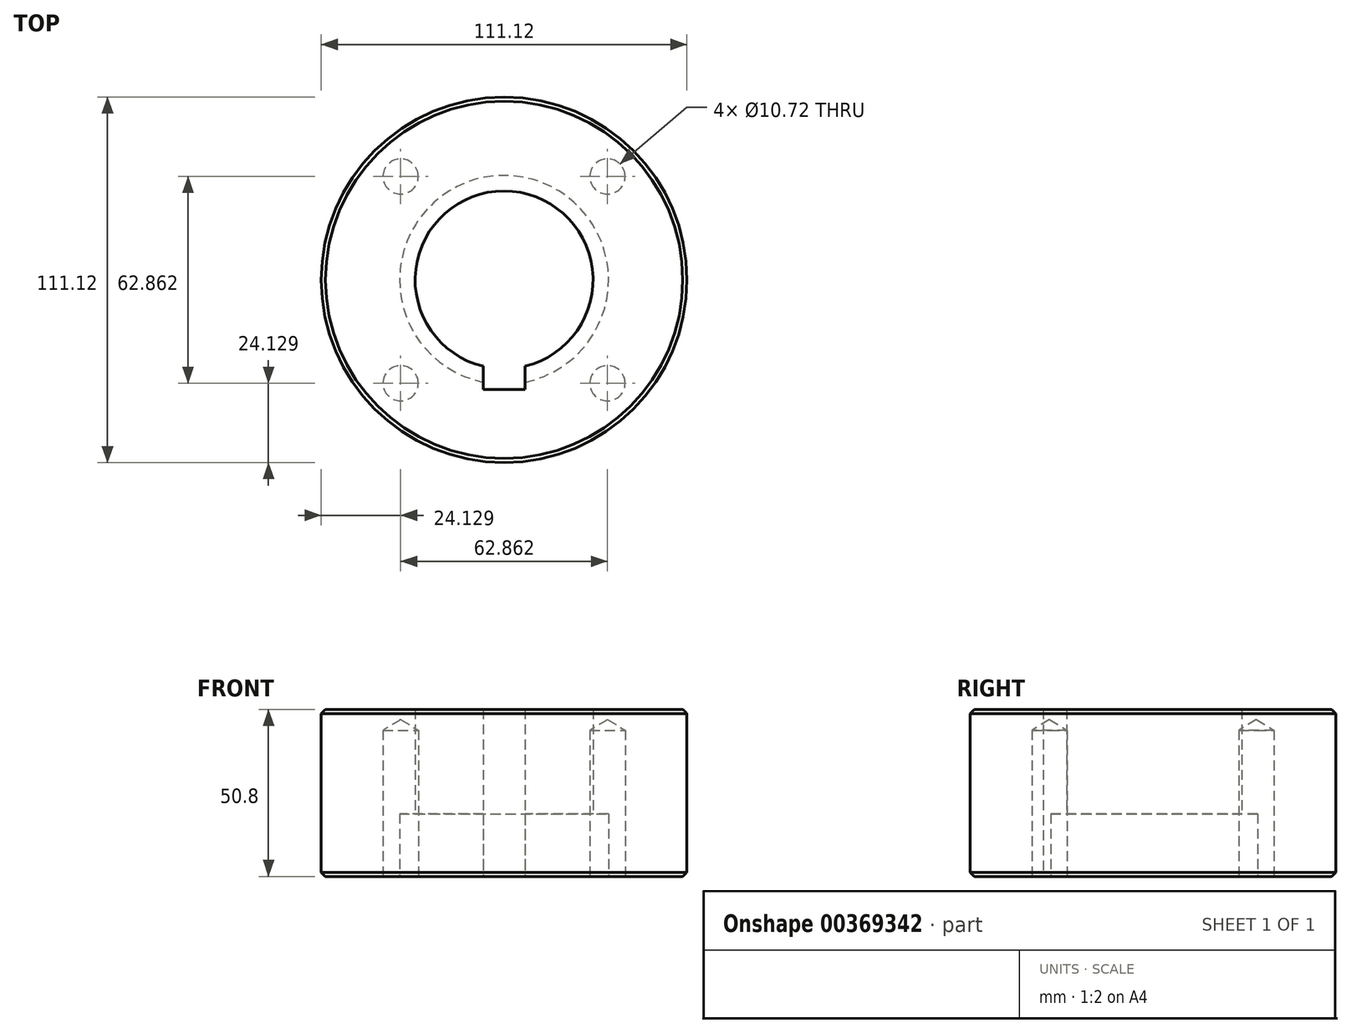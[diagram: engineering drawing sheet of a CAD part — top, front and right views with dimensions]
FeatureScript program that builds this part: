
annotation { "Feature Type Name" : "Feature", "Feature Type Description" : "" }
export const myFeature = defineFeature(function(context is Context, id is Id, definition is map)
    precondition{}
    {
        {
            var Q0;
            Q0=qCreatedBy(makeId("Top.planeOp"),FACE);
            var sketch = newSketch(context, id + "F0", { "sketchPlane" : qUnion([Q0])});
            skCircle(sketch, "E0", {"center": v(0, 0) * mm, "radius": 27.03 * mm});
            skCircle(sketch, "E1", {"center": v(0, 0) * mm, "radius": 55.56 * mm});
            skSolve(sketch);
        }
        {
            var Q0;
            Q0=qSketchRegion(id+"F0",true);
            extrude(context, id + "F1", {"entities" : qUnion([Q0]), "depth" : 50.8 * mm});
        }
        {
            var Q0;
            Q0=makeQuery(id+"F1.opExtrude","CAP_FACE",FACE,{"disambiguationData":[OSD([sQuery(id+"F0.wireOp",EDGE,"E0"),sQuery(id+"F0.wireOp",EDGE,"E1")])],"isStart":true});
            var sketch = newSketch(context, id + "F2", { "sketchPlane" : qUnion([Q0])});
            skPoint(sketch, "E2.center", {"position": v(0, 0) * mm});
            skLineSegment(sketch, "E3", {"start": v(0, 0) * mm, "end": v(0, 89.06) * mm});
            skLineSegment(sketch, "E4", {"start": v(0, 0) * mm, "end": v(67.76, 67.76) * mm});
            skPoint(sketch, "E5", {"position": v(31.43, 31.43) * mm});
            skPoint(sketch, "E6.1.0", {"position": v(-31.43, 31.43) * mm});
            skPoint(sketch, "E6.2.0", {"position": v(-31.43, -31.43) * mm});
            skPoint(sketch, "E6.3.0", {"position": v(31.43, -31.43) * mm});
            skSolve(sketch);
        }
        {
            var Q0;
            Q0=makeQuery(id+"F1.opExtrude","CAP_FACE",FACE,{"disambiguationData":[OSD([sQuery(id+"F0.wireOp",EDGE,"E0"),sQuery(id+"F0.wireOp",EDGE,"E1")])],"isStart":true});
            var sketch = newSketch(context, id + "F3", { "sketchPlane" : qUnion([Q0])});
            skCircle(sketch, "E7", {"center": v(0, 0) * mm, "radius": 31.75 * mm});
            skSolve(sketch);
        }
        {
            var Q0;
            Q0=qSketchRegion(id+"F3",true);
            extrude(context, id + "F4", {"entities" : qUnion([Q0]), "operationType" : NewBodyOperationType.REMOVE, "oppositeDirection" : true, "depth" : 19.05 * mm});
        }
        {
            var Q0;
            Q0=makeQuery(id+"F1.opExtrude","CAP_FACE",FACE,{"disambiguationData":[OSD([sQuery(id+"F0.wireOp",EDGE,"E0"),sQuery(id+"F0.wireOp",EDGE,"E1")])],"isStart":true});
            var sketch = newSketch(context, id + "F5", { "sketchPlane" : qUnion([Q0])});
            skLineSegment(sketch, "E8", {"start": v(-72.6, 0) * mm, "end": v(-72.6, 33.34) * mm});
            skLineSegment(sketch, "E9", {"start": v(-72.6, 33.34) * mm, "end": v(82.29, 33.34) * mm});
            skLineSegment(sketch, "E10.bottom", {"start": v(-6.35, 33.34) * mm, "end": v(6.35, 33.34) * mm});
            skLineSegment(sketch, "E10.left", {"start": v(-6.35, 33.34) * mm, "end": v(-6.35, 0) * mm});
            skLineSegment(sketch, "E10.right", {"start": v(6.35, 33.34) * mm, "end": v(6.35, 0) * mm});
            skPoint(sketch, "E10.middle", {"position": v(0, 0) * mm});
            skLineSegment(sketch, "E11", {"start": v(-6.35, 0) * mm, "end": v(6.35, 0) * mm});
            skPoint(sketch, "E12.orphan", {"position": v(-6.35, -33.34) * mm});
            skPoint(sketch, "E13.orphan", {"position": v(6.35, -33.34) * mm});
            skSolve(sketch);
        }
        {
            var Q0;
            Q0=qSketchRegion(id+"F5",true);
            extrude(context, id + "F6", {"entities" : qUnion([Q0]), "operationType" : NewBodyOperationType.REMOVE, "endBound" : BoundingType.THROUGH_ALL, "oppositeDirection" : true, "depth" : 25.4 * mm});
        }
        {
            var Q0;
            Q0=makeQuery(id+"F1.opExtrude","CAP_EDGE",EDGE,{"disambiguationData":[OSD([sQuery(id+"F0.wireOp",EDGE,"E1")])],"isStart":false});
            var Q1;
            Q1=makeQuery(id+"F1.opExtrude","CAP_EDGE",EDGE,{"disambiguationData":[OSD([sQuery(id+"F0.wireOp",EDGE,"E1")])],"isStart":true});
            chamfer(context, id + "F7", {"entities" : qUnion([Q0, Q1]), "width" : 1.27 * mm, "tangentPropagation" : true});
        }
        {
            var Q0;
            Q0=sQuery(id+"F2.wireOp",VERTEX,"E6.2.0");
            var Q1;
            Q1=sQuery(id+"F2.wireOp",VERTEX,"E6.1.0");
            var Q2;
            Q2=sQuery(id+"F2.wireOp",VERTEX,"E5");
            var Q3;
            Q3=sQuery(id+"F2.wireOp",VERTEX,"E6.3.0");
            var Q4;
            Q4=makeQuery(id+"F1.opExtrude","SWEPT_BODY",BODY,{"disambiguationData":[OSD([sQuery(id+"F0.wireOp",EDGE,"E0"),sQuery(id+"F0.wireOp",EDGE,"E1")])]});
            hole(context, id + "F8", {"style" : HoleStyle.SIMPLE, "endStyle" : HoleEndStyle.BLIND, "standardTappedOrClearance" : lookupTablePath({ "standard" : "ANSI", "engagement" : "75%", "pitch" : "13 tpi", "size" : "1/2", "type" : "Tapped" }), "standardBlindInLast" : lookupTablePath({ "standard" : "ANSI", "engagement" : "75%", "pitch" : "13 tpi", "size" : "1/2", "type" : "Tapped" }), "holeDiameter" : 10.72 * mm, "showTappedDepth" : true, "holeDepth" : 44.45 * mm, "isTappedThrough" : true, "tappedDepth" : 38.6 * mm, "tapClearance" : 3, "startFromSketch" : true, "locations" : qUnion([Q0, Q1, Q2, Q3]), "scope" : qUnion([Q4]), "majorDiameter" : 12.7 * mm});
        }
    });
